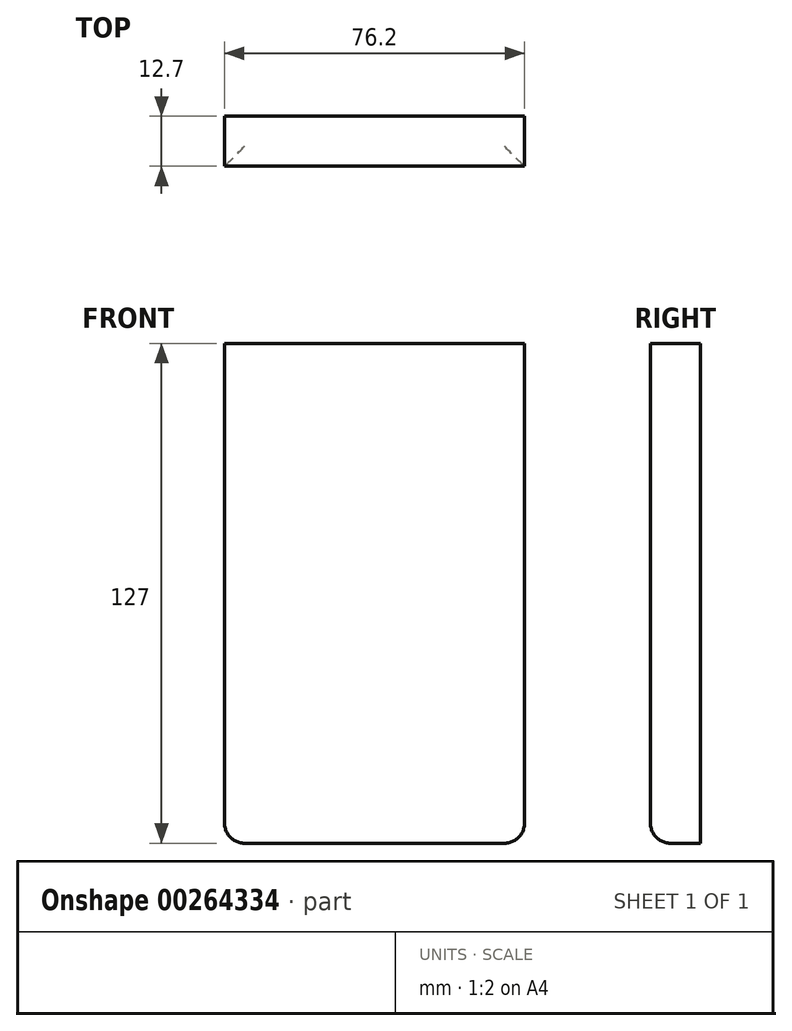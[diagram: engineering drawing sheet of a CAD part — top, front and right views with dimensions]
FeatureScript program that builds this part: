
annotation { "Feature Type Name" : "Feature", "Feature Type Description" : "" }
export const myFeature = defineFeature(function(context is Context, id is Id, definition is map)
    precondition{}
    {
        {
            var Q0;
            Q0=qCreatedBy(makeId("Front.planeOp"),FACE);
            var sketch = newSketch(context, id + "F0", { "sketchPlane" : qUnion([Q0])});
            skLineSegment(sketch, "E0.bottom", {"start": v(38.1, 63.5) * mm, "end": v(-38.1, 63.5) * mm});
            skLineSegment(sketch, "E0.top", {"start": v(38.1, -63.5) * mm, "end": v(-38.1, -63.5) * mm});
            skLineSegment(sketch, "E0.left", {"start": v(38.1, 63.5) * mm, "end": v(38.1, -63.5) * mm});
            skLineSegment(sketch, "E0.right", {"start": v(-38.1, 63.5) * mm, "end": v(-38.1, -63.5) * mm});
            skPoint(sketch, "E0.middle", {"position": v(0, 0) * mm});
            skSolve(sketch);
        }
        {
            var Q0;
            Q0 = qSketchRegion(id + "F0", true);
            extrude(context, id + "F1", {"entities" : qUnion([Q0]), "depth" : 12.7 * mm});
        }
        {
            var Q0;
            Q0=makeQuery(id+"F1.opExtrude","SWEPT_EDGE",EDGE,{"disambiguationData":[OSD([sQuery(id+"F0.wireOp",EDGE,"E0.top"),sQuery(id+"F0.wireOp",EDGE,"E0.left")])]});
            var Q1;
            Q1=makeQuery(id+"F1.opExtrude","SWEPT_EDGE",EDGE,{"disambiguationData":[OSD([sQuery(id+"F0.wireOp",EDGE,"E0.top"),sQuery(id+"F0.wireOp",EDGE,"E0.right")])]});
            var Q2;
            Q2=makeQuery(id+"F1.opExtrude","CAP_EDGE",EDGE,{"disambiguationData":[OSD([sQuery(id+"F0.wireOp",EDGE,"E0.top")])],"isStart":false});
            fillet(context, id + "F2", {"entities" : qUnion([Q0, Q1, Q2]), "radius" : 5.08 * mm, "tangentPropagation" : true, "allowEdgeOverflow" : false});
        }
    });
